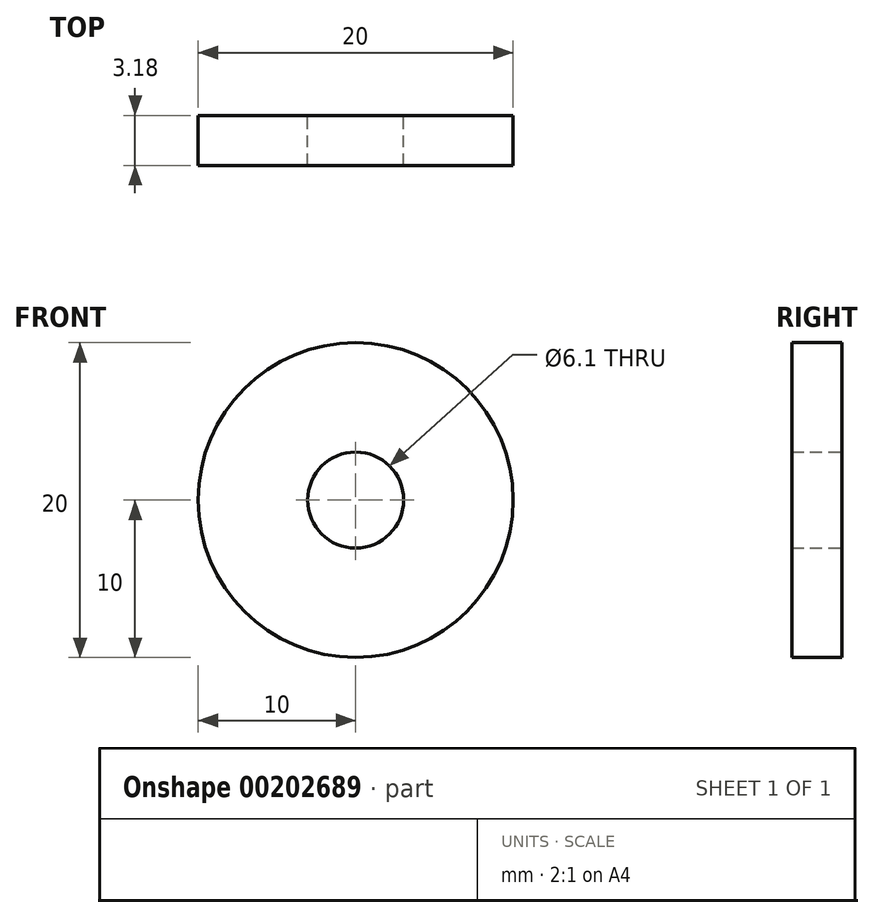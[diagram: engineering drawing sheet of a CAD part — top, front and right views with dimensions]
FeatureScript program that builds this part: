
annotation { "Feature Type Name" : "Feature", "Feature Type Description" : "" }
export const myFeature = defineFeature(function(context is Context, id is Id, definition is map)
    precondition{}
    {
        {
            var Q0;
            Q0=qCreatedBy(makeId("Front.planeOp"),FACE);
            var sketch = newSketch(context, id + "F0", { "sketchPlane" : qUnion([Q0])});
            skCircle(sketch, "E0", {"center": v(0, 0) * mm, "radius": 3.05 * mm});
            skCircle(sketch, "E1", {"center": v(0, 0) * mm, "radius": 10 * mm});
            skSolve(sketch);
        }
        {
            var Q0;
            Q0=makeQuery(id+"F0.imprint","IMPRINT",FACE,{"disambiguationData":[TD([[makeQuery(id+"F0.imprint","IMPRINT",EDGE,{"derivedFrom":sQuery(id+"F0.wireOp",EDGE,"E1")}),1.0]])]});
            var Q1;
            Q1=makeQuery(id+"F0.imprint","IMPRINT",FACE,{"disambiguationData":[TD([[makeQuery(id+"F0.imprint","IMPRINT",EDGE,{"derivedFrom":sQuery(id+"F0.wireOp",EDGE,"E0")}),-1.0]])]});
            extrude(context, id + "F1", {"entities" : qUnion([Q0, Q1]), "depth" : 3.17 * mm});
        }
    });
